# Revit family: IS_UltraFlat_K1618_BIM_DE
name_source: partatom
category: Plumbing Fixtures
revit_build: Autodesk Revit MEP 2016 (Build: 20161004_0715(x64)
units: mm (PartAtom-declared; Revit-internal decimal feet)

## family parameters
Always vertical = Yes
Cut with Voids When Loaded = No
OmniClass Number = 23.45.05.14.17.11
OmniClass Title = Shower Compartments
Part Type = Normal
Room Calculation Point = No
Round Connector Dimension = Use Diameter
Shared = No
Work Plane-Based = No

## types (2) — shared parameters
Accessories = www.idealspec.co.uk
AreaUnits = millimeters
Assembly Code = C1030200
AssetType = Fixed
BIMObjectName = ISI_IdealStandard_ShowerTrays_UltraFlat_K1618
Brand = Ideal Standard
ConnectionType = Plumbing
DrainSize = 90 mm
DurationUnit = year
HasTray = No
Help = www.idealstandard.de
IfcExportAs = IfcSanitaryTerminalType
IfcExportType = SHOWER TRAY
InstallationInstructions = www.idealstandard.de
LinearUnits = millimeters
MaintenanceInformation = www.idealstandard.de
Manufacturer = www.idealstandard.de
ManufacturerURL = www.idealstandard.de
Name = ShowerTrays_UltraFlat_K1618_ISI
NettWeight = 14,50 KG
NominalDepth = 800 mm
NominalHeight = 40 mm
NominalLength = 800 mm
NominalWidth = 800 mm
ProductInformation = www.idealstandard.de
Shape = Sculptured
Size = 40 x 800 x 800 mm
Space = Internal
SpareParts = www.idealstandard.de
URL = www.idealstandard.de
Uniclass2015Code = Pr_40_20_06_84
Uniclass2015Title = Shower trays
Uniclass2015Version = Products v1.1
zero-valued in all types: Cost

## per-type parameters (varying)
| type | BarCode | Color | Description | Features | Finish | MainColor | Model | ModelNumber | ModelReference |
| K161801 - ULTRA FLAT rectangular shower tray 800x800mm | 4015413019125 | White | ULTRA FLAT SHT 80X80 SQ.FLOOREVEN WHITE | ULTRA FLAT SHT 80X80 SQ.FLOOREVEN WHITE | White | White | K161801 | K161801 | ULTRA FLAT SHT 80X80 SQ.FLOOREVEN WHITE |
| K1618YK - ULTRA FLAT rectangular shower tray 800x800mm | 4015413035262 | White Ideal Grip | ULTRA FLAT SHT 80X80 SQ.FLOOREVEN WHITE IDEAL GRIP | ULTRA FLAT SHT 80X80 SQ.FLOOREVEN WHITE IDEAL GRIP | White Ideal Grip | White Ideal Grip | K1618YK | K1618YK | ULTRA FLAT SHT 80X80 SQ.FLOOREVEN WHITE IDEAL GRIP |

## geometry (parser evidence)
native form markers: Blend x4
no freeform markers — native parametric forms only
